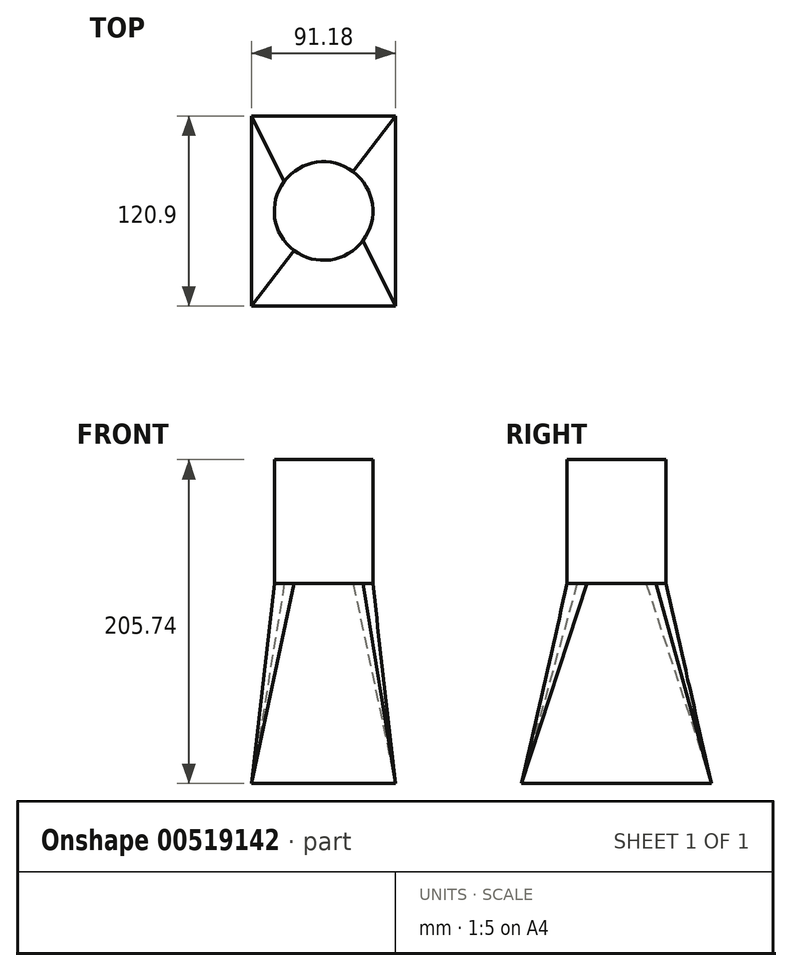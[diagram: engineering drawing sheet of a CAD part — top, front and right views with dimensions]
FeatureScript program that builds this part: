
annotation { "Feature Type Name" : "Feature", "Feature Type Description" : "" }
export const myFeature = defineFeature(function(context is Context, id is Id, definition is map)
    precondition{}
    {
        {
            var Q0;
            Q0=qCreatedBy(makeId("Top.planeOp"),FACE);
            var sketch = newSketch(context, id + "F0", { "sketchPlane" : qUnion([Q0])});
            skLineSegment(sketch, "E0.bottom", {"start": v(45.59, 60.45) * mm, "end": v(-45.59, 60.45) * mm});
            skLineSegment(sketch, "E0.top", {"start": v(45.59, -60.45) * mm, "end": v(-45.59, -60.45) * mm});
            skLineSegment(sketch, "E0.left", {"start": v(45.59, 60.45) * mm, "end": v(45.59, -60.45) * mm});
            skLineSegment(sketch, "E0.right", {"start": v(-45.59, 60.45) * mm, "end": v(-45.59, -60.45) * mm});
            skPoint(sketch, "E0.middle", {"position": v(0, 0) * mm});
            skSolve(sketch);
        }
        {
            var Q0;
            Q0=qCreatedBy(makeId("Top.planeOp"),FACE);
            cPlane(context, id + "F1", {"entities" : qUnion([Q0]), "cplaneType" : CPlaneType.OFFSET, "offset" : 127 * mm, "width" : 152.4 * mm, "height" : 152.4 * mm});
        }
        {
            var Q0;
            Q0=qCreatedBy(id+"F1.planeOp",FACE);
            var sketch = newSketch(context, id + "F2", { "sketchPlane" : qUnion([Q0])});
            skPoint(sketch, "E1.middle", {"position": v(0, 0) * mm});
            skCircle(sketch, "E2", {"center": v(0, 0) * mm, "radius": 31.3 * mm});
            skSolve(sketch);
        }
        {
            var Q0;
            Q0=makeQuery(id+"F2.imprint","IMPRINT",FACE,{"disambiguationData":[TD([[makeQuery(id+"F2.imprint","IMPRINT",EDGE,{"derivedFrom":sQuery(id+"F2.wireOp",EDGE,"E2")}),1.0]])]});
            var Q1;
            Q1=makeQuery(id+"F0.imprint","IMPRINT",FACE,{"disambiguationData":[TD([[makeQuery(id+"F0.imprint","IMPRINT",EDGE,{"derivedFrom":sQuery(id+"F0.wireOp",EDGE,"E0.bottom")}),1.0]])]});
            loft(context, id + "F3", {"sheetProfilesArray" : [{ "sheetProfileEntities" : qUnion([Q0]) }, { "sheetProfileEntities" : qUnion([Q1]) }]});
        }
        {
            var Q0;
            Q0=makeQuery(id+"F3.opLoft","CAP_FACE",FACE,{"disambiguationData":[OSD([makeQuery(id+"F2.imprint","IMPRINT",FACE,{"disambiguationData":[TD([[makeQuery(id+"F2.imprint","IMPRINT",EDGE,{"derivedFrom":sQuery(id+"F2.wireOp",EDGE,"E2")}),1.0]])]})])],"isStart":true});
            extrude(context, id + "F4", {"entities" : qUnion([Q0]), "operationType" : NewBodyOperationType.ADD, "depth" : 78.74 * mm});
        }
    });
